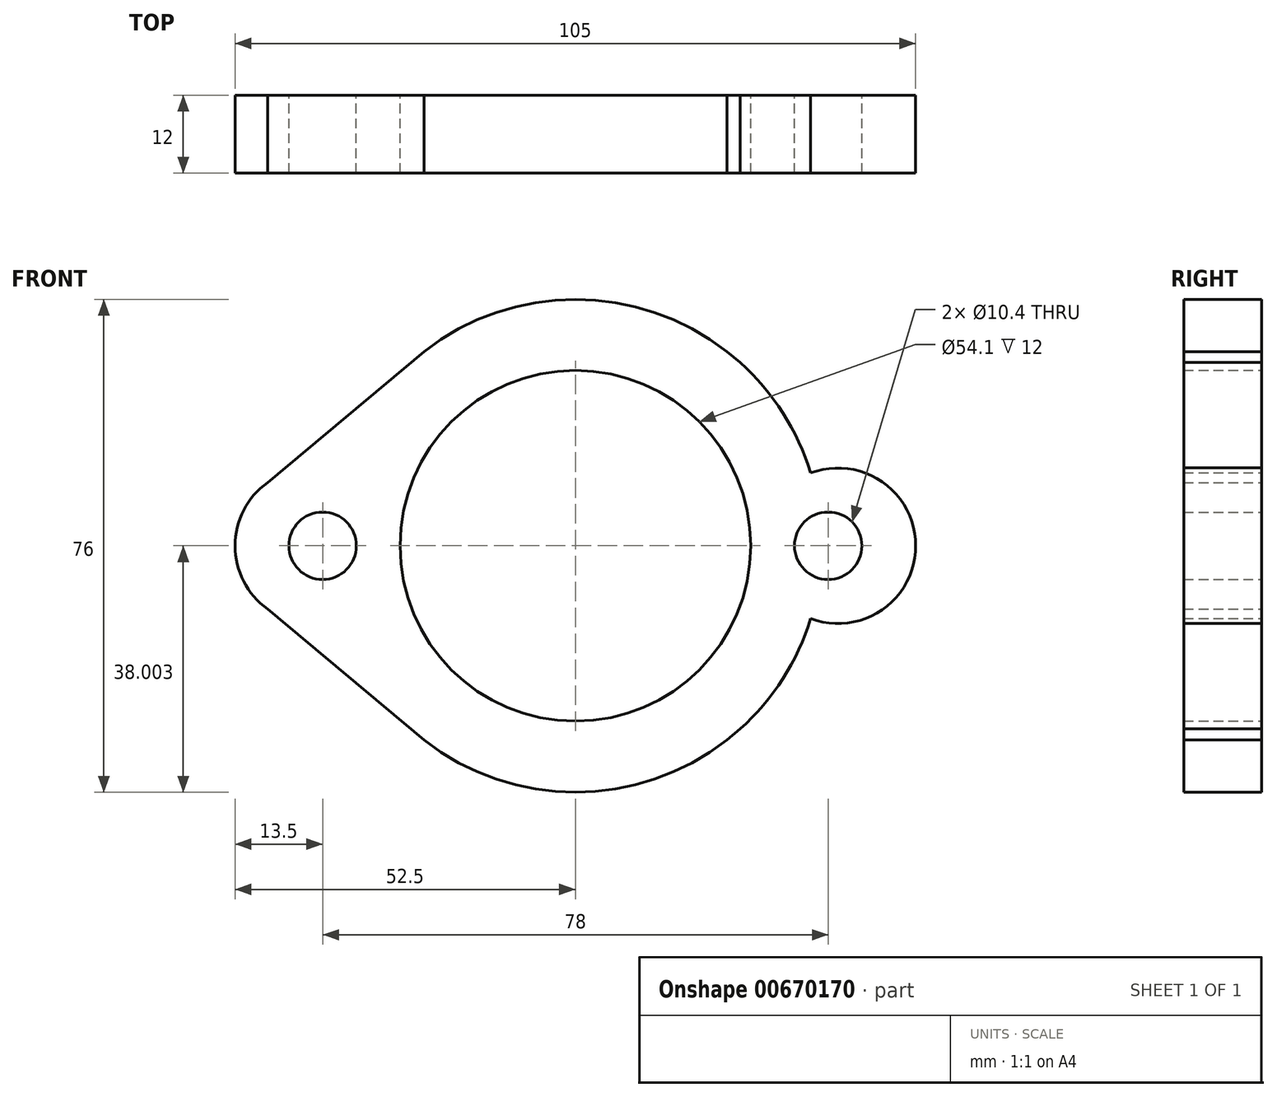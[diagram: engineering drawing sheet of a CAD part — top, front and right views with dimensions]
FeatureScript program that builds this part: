
annotation { "Feature Type Name" : "Feature", "Feature Type Description" : "" }
export const myFeature = defineFeature(function(context is Context, id is Id, definition is map)
    precondition{}
    {
        {
            var Q0;
            Q0=qCreatedBy(makeId("Front.planeOp"),FACE);
            var sketch = newSketch(context, id + "F0", { "sketchPlane" : qUnion([Q0])});
            skCircle(sketch, "E0", {"center": v(-40.93, 197.61) * mm, "radius": 27.05 * mm});
            skLineSegment(sketch, "E1.bottom", {"start": v(-93.43, 159.61) * mm, "end": v(11.57, 159.61) * mm});
            skLineSegment(sketch, "E1.top", {"start": v(-93.43, 235.61) * mm, "end": v(11.57, 235.61) * mm});
            skLineSegment(sketch, "E1.left", {"start": v(-93.43, 159.61) * mm, "end": v(-93.43, 235.61) * mm});
            skLineSegment(sketch, "E1.right", {"start": v(11.57, 159.61) * mm, "end": v(11.57, 235.61) * mm});
            skCircle(sketch, "E2", {"center": v(-79.93, 197.61) * mm, "radius": 5.2 * mm});
            skCircle(sketch, "E3", {"center": v(-1.93, 197.61) * mm, "radius": 5.2 * mm});
            skCircle(sketch, "E4", {"center": v(-40.93, 197.61) * mm, "radius": 39 * mm, "construction": true});
            skCircle(sketch, "E5", {"center": v(-40.93, 197.61) * mm, "radius": 38 * mm});
            skArc(sketch, "E6", {"start": v(-77.23, 208.85) * mm, "mid": v(-93.43, 197.61) * mm, "end": v(-77.23, 186.37) * mm});
            skLineSegment(sketch, "E7", {"start": v(-40.93, 197.61) * mm, "end": v(-40.93, 144.5) * mm, "construction": true});
            skArc(sketch, "E8.MirrorC", {"start": v(-4.63, 208.85) * mm, "mid": v(11.57, 197.61) * mm, "end": v(-4.63, 186.37) * mm});
            skPoint(sketch, "E9", {"position": v(6.57, 197.61) * mm});
            skPoint(sketch, "E9.positionSnap0", {"position": v(11.57, 197.61) * mm});
            skLineSegment(sketch, "E10", {"start": v(6.57, 207.36) * mm, "end": v(-17.55, 227.57) * mm});
            skLineSegment(sketch, "E11", {"start": v(-40.93, 197.61) * mm, "end": v(-25.17, 197.61) * mm, "construction": true});
            skLineSegment(sketch, "E12.MirrorCS", {"start": v(6.57, 187.87) * mm, "end": v(-17.55, 167.65) * mm});
            skLineSegment(sketch, "E13.MirrorCS", {"start": v(-88.43, 187.87) * mm, "end": v(-64.3, 167.65) * mm});
            skLineSegment(sketch, "E14.MirrorCS", {"start": v(-88.43, 207.36) * mm, "end": v(-64.3, 227.57) * mm});
            skSolve(sketch);
        }
        {
            var Q0;
            {var subQ0=sQuery(id+"F0.wireOp",EDGE,"E6");var subQ1=sQuery(id+"F0.wireOp",EDGE,"E5");var subQ2=makeQuery(id+"F0.imprint","INTERSECT",VERTEX,{"disambiguationData":[OD(0.0)],"derivedFrom":[subQ1,subQ0]});Q0=makeQuery(id+"F0.imprint","IMPRINT",FACE,{"disambiguationData":[TD([[makeQuery(id+"F0.imprint","IMPRINT",EDGE,{"disambiguationData":[TD([[subQ2,1.0]])],"derivedFrom":subQ1}),-1.0]])]});}
            var Q1;
            {var subQ1=sQuery(id+"F0.wireOp",EDGE,"E5");var subQ4=sQuery(id+"F0.wireOp",EDGE,"E2");var subQ5=makeQuery(id+"F0.imprint","INTERSECT",VERTEX,{"disambiguationData":[OD(0.0)],"derivedFrom":[subQ4,subQ1]});Q1=makeQuery(id+"F0.imprint","IMPRINT",FACE,{"disambiguationData":[TD([[makeQuery(id+"F0.imprint","IMPRINT",EDGE,{"disambiguationData":[TD([[subQ5,-1.0]])],"derivedFrom":subQ4}),-1.0]])]});}
            var Q2;
            Q2=makeQuery(id+"F0.imprint","IMPRINT",FACE,{"disambiguationData":[TD([[makeQuery(id+"F0.imprint","IMPRINT",EDGE,{"derivedFrom":sQuery(id+"F0.wireOp",EDGE,"E0")}),-1.0]])]});
            var Q3;
            {var subQ0=sQuery(id+"F0.wireOp",EDGE,"E6");var subQ1=sQuery(id+"F0.wireOp",EDGE,"E5");var subQ2=makeQuery(id+"F0.imprint","INTERSECT",VERTEX,{"disambiguationData":[OD(1.0)],"derivedFrom":[subQ1,subQ0]});Q3=makeQuery(id+"F0.imprint","IMPRINT",FACE,{"disambiguationData":[TD([[makeQuery(id+"F0.imprint","IMPRINT",EDGE,{"disambiguationData":[TD([[subQ2,-1.0]])],"derivedFrom":subQ1}),-1.0]])]});}
            var Q4;
            {var subQ0=sQuery(id+"F0.wireOp",EDGE,"E8.MirrorC");var subQ1=sQuery(id+"F0.wireOp",EDGE,"E5");var subQ2=makeQuery(id+"F0.imprint","INTERSECT",VERTEX,{"disambiguationData":[OD(1.0)],"derivedFrom":[subQ1,subQ0]});Q4=makeQuery(id+"F0.imprint","IMPRINT",FACE,{"disambiguationData":[TD([[makeQuery(id+"F0.imprint","IMPRINT",EDGE,{"disambiguationData":[TD([[subQ2,1.0]])],"derivedFrom":subQ1}),-1.0]])]});}
            var Q5;
            {var subQ0=sQuery(id+"F0.wireOp",EDGE,"E8.MirrorC");var subQ1=sQuery(id+"F0.wireOp",EDGE,"E5");var subQ2=makeQuery(id+"F0.imprint","INTERSECT",VERTEX,{"disambiguationData":[OD(0.0)],"derivedFrom":[subQ1,subQ0]});Q5=makeQuery(id+"F0.imprint","IMPRINT",FACE,{"disambiguationData":[TD([[makeQuery(id+"F0.imprint","IMPRINT",EDGE,{"disambiguationData":[TD([[subQ2,-1.0]])],"derivedFrom":subQ1}),-1.0]])]});}
            var Q6;
            {var subQ1=sQuery(id+"F0.wireOp",EDGE,"E5");var subQ4=sQuery(id+"F0.wireOp",EDGE,"E3");var subQ5=makeQuery(id+"F0.imprint","INTERSECT",VERTEX,{"disambiguationData":[OD(0.0)],"derivedFrom":[subQ4,subQ1]});Q6=makeQuery(id+"F0.imprint","IMPRINT",FACE,{"disambiguationData":[TD([[makeQuery(id+"F0.imprint","IMPRINT",EDGE,{"disambiguationData":[TD([[subQ5,1.0]])],"derivedFrom":subQ4}),-1.0]])]});}
            extrude(context, id + "F1", {"entities" : qUnion([Q0, Q1, Q2, Q3, Q4, Q5, Q6]), "depth" : 12 * mm, "offsetDistance" : 25 * mm});
        }
    });
